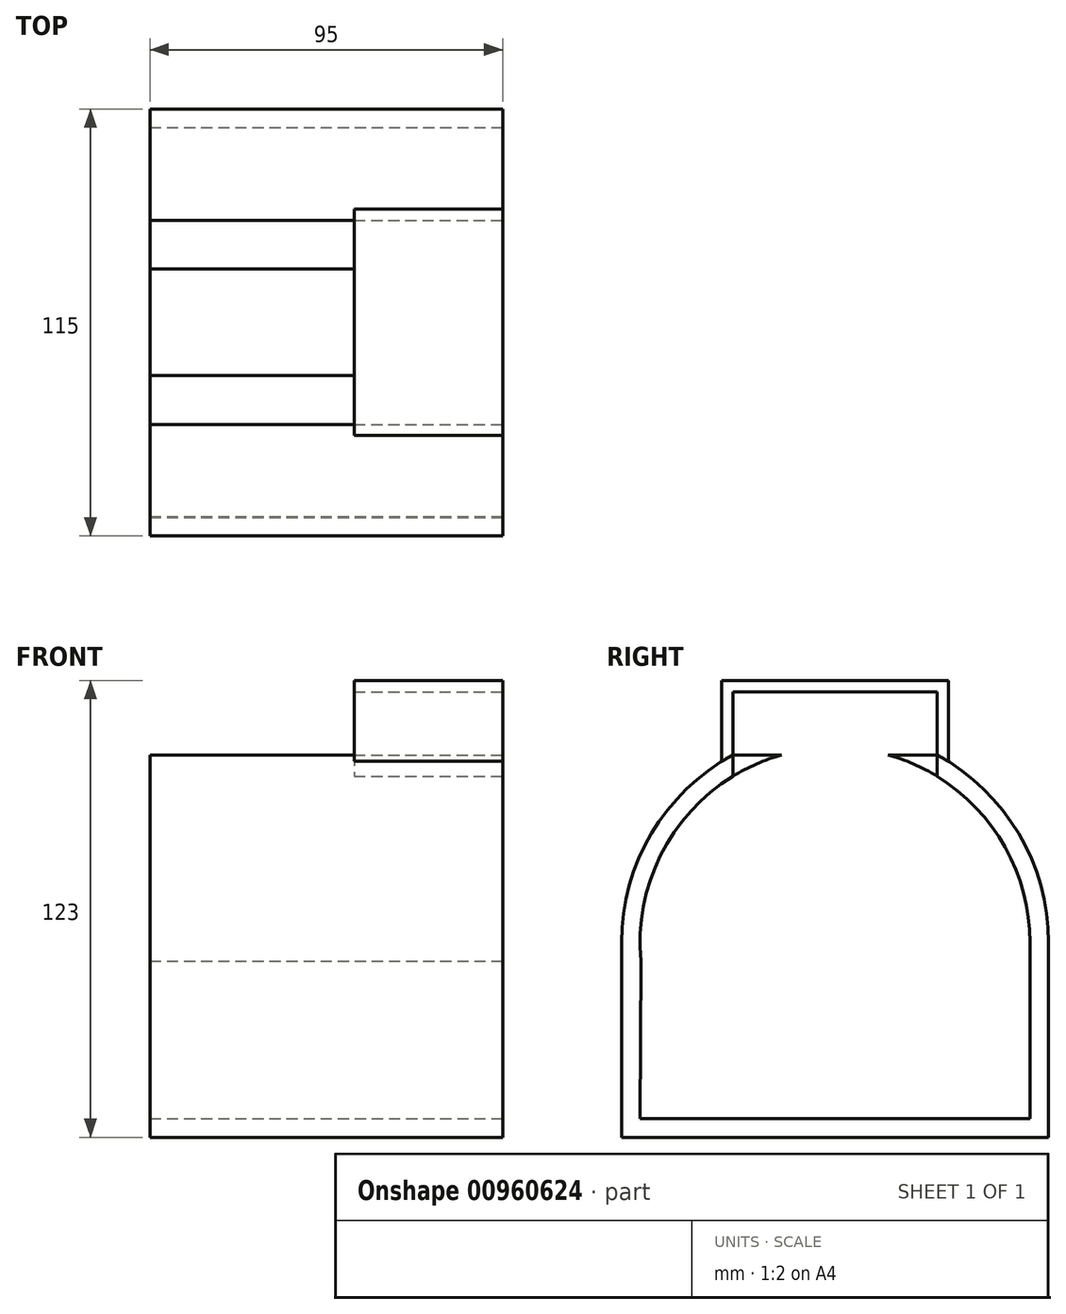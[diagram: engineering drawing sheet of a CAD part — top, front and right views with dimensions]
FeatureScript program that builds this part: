
annotation { "Feature Type Name" : "Feature", "Feature Type Description" : "" }
export const myFeature = defineFeature(function(context is Context, id is Id, definition is map)
    precondition{}
    {
        {
            var Q0;
            Q0=qCreatedBy(makeId("Right.planeOp"),FACE);
            var sketch = newSketch(context, id + "F0", { "sketchPlane" : qUnion([Q0])});
            skLineSegment(sketch, "E0.bottom", {"start": v(0, 0) * mm, "end": v(115, 0) * mm});
            skLineSegment(sketch, "E0.top", {"start": v(0, 110) * mm, "end": v(115, 110) * mm});
            skLineSegment(sketch, "E0.left", {"start": v(0, 0) * mm, "end": v(0, 110) * mm});
            skLineSegment(sketch, "E0.right", {"start": v(115, 0) * mm, "end": v(115, 110) * mm});
            skCircle(sketch, "E1", {"center": v(57.5, 52.5) * mm, "radius": 57.5 * mm});
            skLineSegment(sketch, "E2", {"start": v(57.5, 0) * mm, "end": v(57.5, 52.5) * mm, "construction": true});
            skCircle(sketch, "E3", {"center": v(57.5, 52.5) * mm, "radius": 52.5 * mm});
            skLineSegment(sketch, "E4", {"start": v(5, 0) * mm, "end": v(5.24, 47.5) * mm});
            skLineSegment(sketch, "E5", {"start": v(110, 52.5) * mm, "end": v(110, 0) * mm});
            skLineSegment(sketch, "E6", {"start": v(0, 5) * mm, "end": v(115, 5) * mm});
            skLineSegment(sketch, "E7.bottom", {"start": v(30, 103) * mm, "end": v(85, 103) * mm});
            skLineSegment(sketch, "E7.top", {"start": v(30, 120) * mm, "end": v(85, 120) * mm});
            skLineSegment(sketch, "E7.left", {"start": v(30, 103) * mm, "end": v(30, 120) * mm});
            skLineSegment(sketch, "E7.right", {"start": v(85, 103) * mm, "end": v(85, 120) * mm});
            skLineSegment(sketch, "E8.top", {"start": v(27, 123) * mm, "end": v(88, 123) * mm});
            skLineSegment(sketch, "E8.left", {"start": v(27, 101.24) * mm, "end": v(27, 123) * mm});
            skLineSegment(sketch, "E8.right", {"start": v(88, 101.24) * mm, "end": v(88, 123) * mm});
            skLineSegment(sketch, "E9", {"start": v(30, 103) * mm, "end": v(30, 97.22) * mm});
            skLineSegment(sketch, "E10", {"start": v(85, 103) * mm, "end": v(85, 97.22) * mm});
            skSolve(sketch);
        }
        {
            var Q0;
            {var subQ0=sQuery(id+"F0.wireOp",EDGE,"E1");var subQ4=sQuery(id+"F0.wireOp",EDGE,"E0.bottom");var subQ5=makeQuery(id+"F0.imprint","INTERSECT",VERTEX,{"disambiguationData":[OD(0.0)],"derivedFrom":[subQ4,subQ0]});Q0=makeQuery(id+"F0.imprint","IMPRINT",FACE,{"disambiguationData":[TD([[makeQuery(id+"F0.imprint","IMPRINT",EDGE,{"disambiguationData":[TD([[subQ5,-1.0]])],"derivedFrom":subQ4}),1.0]])]});}
            var Q1;
            {var subQ0=sQuery(id+"F0.wireOp",EDGE,"E0.right");var subQ1=sQuery(id+"F0.wireOp",EDGE,"E0.bottom");var subQ2=makeQuery(id+"F0.imprint","INTERSECT",VERTEX,{"derivedFrom":[subQ1,subQ0]});Q1=makeQuery(id+"F0.imprint","IMPRINT",FACE,{"disambiguationData":[TD([[makeQuery(id+"F0.imprint","IMPRINT",EDGE,{"disambiguationData":[TD([[subQ2,1.0]])],"derivedFrom":subQ1}),1.0]])]});}
            var Q2;
            {var subQ0=sQuery(id+"F0.wireOp",EDGE,"E4");var subQ1=sQuery(id+"F0.wireOp",EDGE,"E0.bottom");var subQ2=makeQuery(id+"F0.imprint","INTERSECT",VERTEX,{"derivedFrom":[subQ1,subQ0]});Q2=makeQuery(id+"F0.imprint","IMPRINT",FACE,{"disambiguationData":[TD([[makeQuery(id+"F0.imprint","IMPRINT",EDGE,{"disambiguationData":[TD([[subQ2,-1.0]])],"derivedFrom":subQ1}),1.0]])]});}
            var Q3;
            {var subQ0=sQuery(id+"F0.wireOp",EDGE,"E3");var subQ1=sQuery(id+"F0.wireOp",EDGE,"E0.bottom");var subQ2=makeQuery(id+"F0.imprint","INTERSECT",VERTEX,{"disambiguationData":[OD(0.0)],"derivedFrom":[subQ1,subQ0]});Q3=makeQuery(id+"F0.imprint","IMPRINT",FACE,{"disambiguationData":[TD([[makeQuery(id+"F0.imprint","IMPRINT",EDGE,{"disambiguationData":[TD([[subQ2,-1.0]])],"derivedFrom":subQ1}),1.0]])]});}
            var Q4;
            {var subQ0=sQuery(id+"F0.wireOp",EDGE,"E5");var subQ1=sQuery(id+"F0.wireOp",EDGE,"E0.bottom");var subQ2=makeQuery(id+"F0.imprint","INTERSECT",VERTEX,{"derivedFrom":[subQ1,subQ0]});Q4=makeQuery(id+"F0.imprint","IMPRINT",FACE,{"disambiguationData":[TD([[makeQuery(id+"F0.imprint","IMPRINT",EDGE,{"disambiguationData":[TD([[subQ2,1.0]])],"derivedFrom":subQ1}),1.0]])]});}
            var Q5;
            {var subQ0=sQuery(id+"F0.wireOp",EDGE,"E1");var subQ1=sQuery(id+"F0.wireOp",EDGE,"E0.bottom");var subQ2=makeQuery(id+"F0.imprint","INTERSECT",VERTEX,{"disambiguationData":[OD(1.0)],"derivedFrom":[subQ1,subQ0]});Q5=makeQuery(id+"F0.imprint","IMPRINT",FACE,{"disambiguationData":[TD([[makeQuery(id+"F0.imprint","IMPRINT",EDGE,{"disambiguationData":[TD([[subQ2,1.0]])],"derivedFrom":subQ1}),1.0]])]});}
            var Q6;
            {var subQ0=sQuery(id+"F0.wireOp",EDGE,"E6");var subQ1=sQuery(id+"F0.wireOp",EDGE,"E0.right");var subQ2=makeQuery(id+"F0.imprint","INTERSECT",VERTEX,{"derivedFrom":[subQ1,subQ0]});Q6=makeQuery(id+"F0.imprint","IMPRINT",FACE,{"disambiguationData":[TD([[makeQuery(id+"F0.imprint","IMPRINT",EDGE,{"disambiguationData":[TD([[subQ2,-1.0]])],"derivedFrom":subQ1}),1.0]])]});}
            var Q7;
            {var subQ0=sQuery(id+"F0.wireOp",EDGE,"E6");var subQ1=sQuery(id+"F0.wireOp",EDGE,"E0.left");var subQ2=makeQuery(id+"F0.imprint","INTERSECT",VERTEX,{"derivedFrom":[subQ1,subQ0]});Q7=makeQuery(id+"F0.imprint","IMPRINT",FACE,{"disambiguationData":[TD([[makeQuery(id+"F0.imprint","IMPRINT",EDGE,{"disambiguationData":[TD([[subQ2,-1.0]])],"derivedFrom":subQ1}),-1.0]])]});}
            var Q8;
            {var subQ0=sQuery(id+"F0.wireOp",EDGE,"E0.left");var subQ1=sQuery(id+"F0.wireOp",EDGE,"E0.bottom");var subQ2=makeQuery(id+"F0.imprint","INTERSECT",VERTEX,{"derivedFrom":[subQ1,subQ0]});Q8=makeQuery(id+"F0.imprint","IMPRINT",FACE,{"disambiguationData":[TD([[makeQuery(id+"F0.imprint","IMPRINT",EDGE,{"disambiguationData":[TD([[subQ2,-1.0]])],"derivedFrom":subQ1}),1.0]])]});}
            var Q9;
            {var subQ0=sQuery(id+"F0.wireOp",EDGE,"E3");var subQ1=makeQuery(id+"F0.imprint","INTERSECT",VERTEX,{"derivedFrom":[sQuery(id+"F0.wireOp",EDGE,"E0.bottom"),subQ0]});Q9=makeQuery(id+"F0.imprint","IMPRINT",FACE,{"disambiguationData":[TD([[makeQuery(id+"F0.imprint","IMPRINT",EDGE,{"disambiguationData":[TD([[subQ1,1.0]])],"derivedFrom":subQ0}),1.0]])]});}
            var Q10;
            {var subQ3=sQuery(id+"F0.wireOp",EDGE,"E1");var subQ5=makeQuery(id+"F0.imprint","INTERSECT",VERTEX,{"derivedFrom":[sQuery(id+"F0.wireOp",EDGE,"E0.left"),subQ3]});Q10=makeQuery(id+"F0.imprint","IMPRINT",FACE,{"disambiguationData":[TD([[makeQuery(id+"F0.imprint","IMPRINT",EDGE,{"disambiguationData":[TD([[subQ5,-1.0]])],"derivedFrom":subQ3}),1.0]])]});}
            var Q11;
            {var subQ3=sQuery(id+"F0.wireOp",EDGE,"E1");var subQ5=makeQuery(id+"F0.imprint","INTERSECT",VERTEX,{"derivedFrom":[sQuery(id+"F0.wireOp",EDGE,"E0.right"),subQ3]});Q11=makeQuery(id+"F0.imprint","IMPRINT",FACE,{"disambiguationData":[TD([[makeQuery(id+"F0.imprint","IMPRINT",EDGE,{"disambiguationData":[TD([[subQ5,1.0]])],"derivedFrom":subQ3}),1.0]])]});}
            var Q12;
            {var subQ0=sQuery(id+"F0.wireOp",EDGE,"E7.bottom");var subQ3=sQuery(id+"F0.wireOp",EDGE,"E3");var subQ7=makeQuery(id+"F0.imprint","INTERSECT",VERTEX,{"disambiguationData":[OD(0.0)],"derivedFrom":[subQ3,subQ0]});Q12=makeQuery(id+"F0.imprint","IMPRINT",FACE,{"disambiguationData":[TD([[makeQuery(id+"F0.imprint","IMPRINT",EDGE,{"disambiguationData":[TD([[subQ7,-1.0]])],"derivedFrom":subQ3}),-1.0]])]});}
            var Q13;
            {var subQ0=sQuery(id+"F0.wireOp",EDGE,"E9");Q13=makeQuery(id+"F0.imprint","IMPRINT",FACE,{"disambiguationData":[TD([[makeQuery(id+"F0.imprint","IMPRINT",EDGE,{"derivedFrom":subQ0}),1.0]])]});}
            var Q14;
            {var subQ0=sQuery(id+"F0.wireOp",EDGE,"E10");Q14=makeQuery(id+"F0.imprint","IMPRINT",FACE,{"disambiguationData":[TD([[makeQuery(id+"F0.imprint","IMPRINT",EDGE,{"derivedFrom":subQ0}),-1.0]])]});}
            extrude(context, id + "F1", {"entities" : qUnion([Q0, Q1, Q2, Q3, Q4, Q5, Q6, Q7, Q8, Q9, Q10, Q11, Q12, Q13, Q14]), "oppositeDirection" : true, "depth" : 95 * mm, "offsetDistance" : 25 * mm});
        }
        {
            var Q0;
            {var subQ1=sQuery(id+"F0.wireOp",EDGE,"E7.top");Q0=makeQuery(id+"F0.imprint","IMPRINT",FACE,{"disambiguationData":[TD([[makeQuery(id+"F0.imprint","IMPRINT",EDGE,{"derivedFrom":subQ1}),1.0]])]});}
            var Q1;
            {var subQ0=sQuery(id+"F0.wireOp",EDGE,"E8.left");var subQ1=sQuery(id+"F0.wireOp",EDGE,"E0.top");var subQ2=makeQuery(id+"F0.imprint","INTERSECT",VERTEX,{"derivedFrom":[subQ1,subQ0]});Q1=makeQuery(id+"F0.imprint","IMPRINT",FACE,{"disambiguationData":[TD([[makeQuery(id+"F0.imprint","IMPRINT",EDGE,{"disambiguationData":[TD([[subQ2,-1.0]])],"derivedFrom":subQ1}),-1.0]])]});}
            var Q2;
            {var subQ0=sQuery(id+"F0.wireOp",EDGE,"E8.right");var subQ1=sQuery(id+"F0.wireOp",EDGE,"E0.top");var subQ2=makeQuery(id+"F0.imprint","INTERSECT",VERTEX,{"derivedFrom":[subQ1,subQ0]});Q2=makeQuery(id+"F0.imprint","IMPRINT",FACE,{"disambiguationData":[TD([[makeQuery(id+"F0.imprint","IMPRINT",EDGE,{"disambiguationData":[TD([[subQ2,1.0]])],"derivedFrom":subQ1}),-1.0]])]});}
            extrude(context, id + "F2", {"entities" : qUnion([Q0, Q1, Q2]), "oppositeDirection" : true, "depth" : 40 * mm, "offsetDistance" : 25 * mm});
        }
        {
            var Q0;
            {var subQ0=sQuery(id+"F0.wireOp",EDGE,"E7.bottom");var subQ3=sQuery(id+"F0.wireOp",EDGE,"E3");var subQ7=makeQuery(id+"F0.imprint","INTERSECT",VERTEX,{"disambiguationData":[OD(0.0)],"derivedFrom":[subQ3,subQ0]});Q0=makeQuery(id+"F0.imprint","IMPRINT",FACE,{"disambiguationData":[TD([[makeQuery(id+"F0.imprint","IMPRINT",EDGE,{"disambiguationData":[TD([[subQ7,-1.0]])],"derivedFrom":subQ3}),-1.0]])]});}
            var Q1;
            {var subQ0=sQuery(id+"F0.wireOp",EDGE,"E9");Q1=makeQuery(id+"F0.imprint","IMPRINT",FACE,{"disambiguationData":[TD([[makeQuery(id+"F0.imprint","IMPRINT",EDGE,{"derivedFrom":subQ0}),1.0]])]});}
            var Q2;
            {var subQ0=sQuery(id+"F0.wireOp",EDGE,"E10");Q2=makeQuery(id+"F0.imprint","IMPRINT",FACE,{"disambiguationData":[TD([[makeQuery(id+"F0.imprint","IMPRINT",EDGE,{"derivedFrom":subQ0}),-1.0]])]});}
            extrude(context, id + "F3", {"entities" : qUnion([Q0, Q1, Q2]), "operationType" : NewBodyOperationType.REMOVE, "oppositeDirection" : true, "depth" : 40 * mm, "offsetDistance" : 25 * mm});
        }
    });
